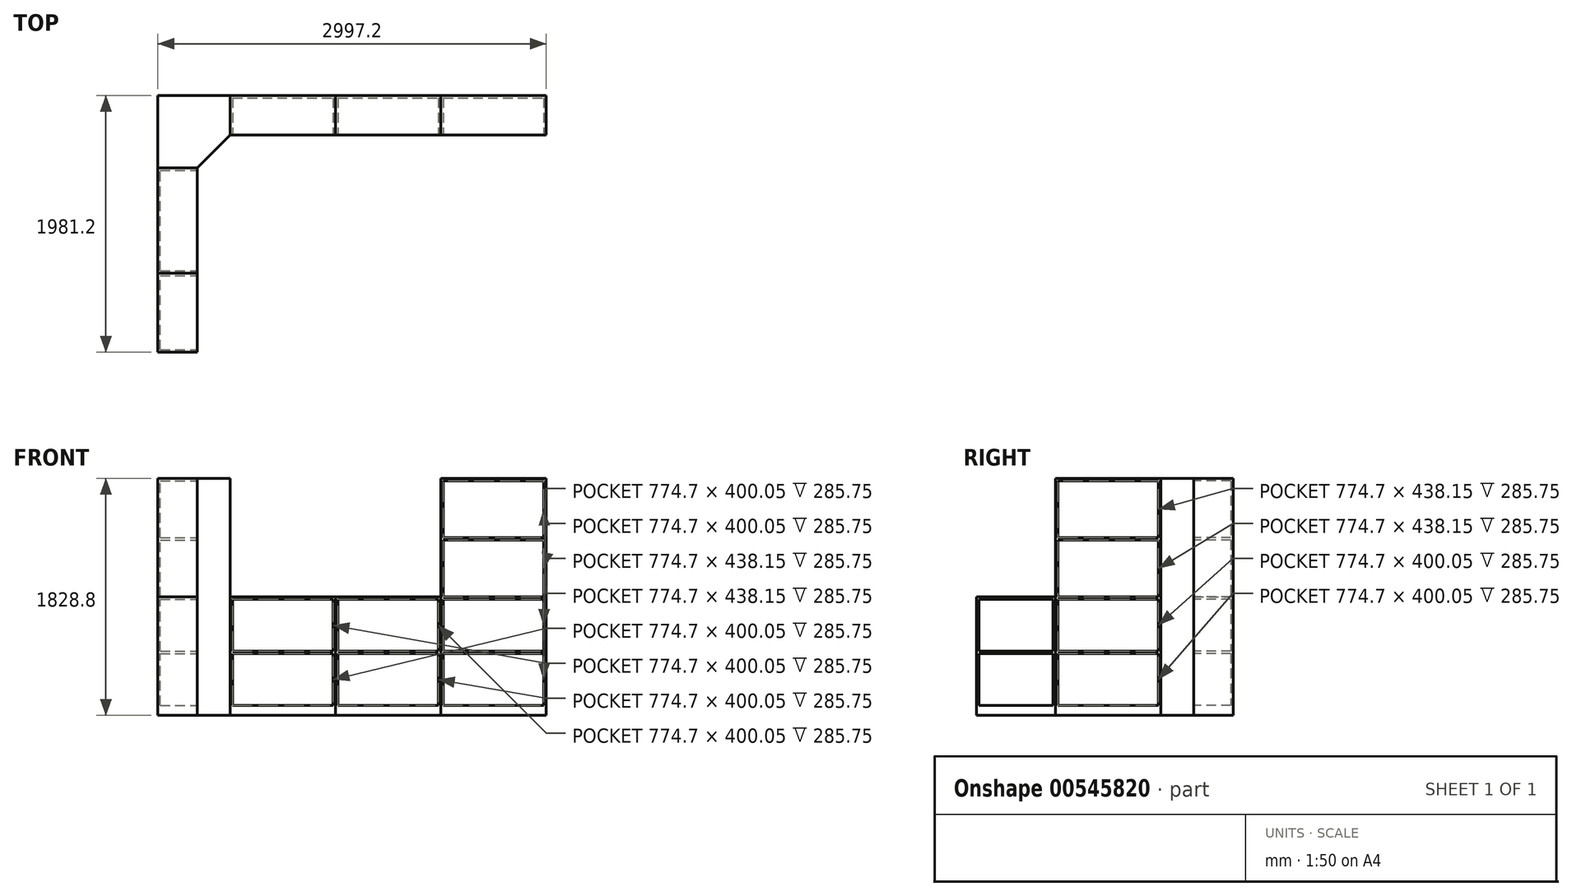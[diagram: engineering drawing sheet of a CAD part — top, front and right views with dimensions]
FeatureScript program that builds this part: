
annotation { "Feature Type Name" : "Feature", "Feature Type Description" : "" }
export const myFeature = defineFeature(function(context is Context, id is Id, definition is map)
    precondition{}
    {
        {
            var Q0;
            Q0=qCreatedBy(makeId("Top.planeOp"),FACE);
            var sketch = newSketch(context, id + "F0", { "sketchPlane" : qUnion([Q0])});
            skLineSegment(sketch, "E0", {"start": v(0, 0) * mm, "end": v(2997.2, 0) * mm});
            skLineSegment(sketch, "E1", {"start": v(0, 0) * mm, "end": v(0, -1981.2) * mm});
            skLineSegment(sketch, "E2", {"start": v(2997.2, 0) * mm, "end": v(2997.2, -304.8) * mm});
            skLineSegment(sketch, "E3", {"start": v(2997.2, -304.8) * mm, "end": v(2184.4, -304.8) * mm});
            skLineSegment(sketch, "E4", {"start": v(2184.4, -304.8) * mm, "end": v(2184.4, 0) * mm});
            skLineSegment(sketch, "E5", {"start": v(2184.4, -304.8) * mm, "end": v(1371.6, -304.8) * mm});
            skLineSegment(sketch, "E6", {"start": v(1371.6, -304.8) * mm, "end": v(1371.6, 0) * mm});
            skLineSegment(sketch, "E7", {"start": v(1371.6, -304.8) * mm, "end": v(558.8, -304.8) * mm});
            skLineSegment(sketch, "E8", {"start": v(558.8, -304.8) * mm, "end": v(558.8, 0) * mm});
            skLineSegment(sketch, "E9", {"start": v(0, -1981.2) * mm, "end": v(304.8, -1981.2) * mm});
            skLineSegment(sketch, "E10", {"start": v(304.8, -1981.2) * mm, "end": v(304.8, -1371.6) * mm});
            skLineSegment(sketch, "E11", {"start": v(304.8, -1371.6) * mm, "end": v(0, -1371.6) * mm});
            skLineSegment(sketch, "E12", {"start": v(304.8, -558.8) * mm, "end": v(0, -558.8) * mm});
            skLineSegment(sketch, "E13", {"start": v(304.8, -1371.6) * mm, "end": v(304.8, -1371.6) * mm});
            skLineSegment(sketch, "E14", {"start": v(304.8, -1371.6) * mm, "end": v(304.8, -558.8) * mm});
            skLineSegment(sketch, "E15", {"start": v(304.8, -558.8) * mm, "end": v(558.8, -304.8) * mm});
            skSolve(sketch);
        }
        {
            var Q0;
            {var subQ0=sQuery(id+"F0.wireOp",EDGE,"E9");Q0=makeQuery(id+"F0.imprint","IMPRINT",FACE,{"disambiguationData":[TD([[makeQuery(id+"F0.imprint","IMPRINT",EDGE,{"derivedFrom":subQ0}),1.0]])]});}
            extrude(context, id + "F1", {"entities" : qUnion([Q0]), "depth" : 914.4 * mm, "offsetDistance" : 25.4 * mm});
        }
        {
            var Q0;
            {var subQ0=sQuery(id+"F0.wireOp",EDGE,"E11");Q0=makeQuery(id+"F0.imprint","IMPRINT",FACE,{"disambiguationData":[TD([[makeQuery(id+"F0.imprint","IMPRINT",EDGE,{"derivedFrom":subQ0}),-1.0]])]});}
            extrude(context, id + "F2", {"entities" : qUnion([Q0]), "depth" : 1828.8 * mm, "offsetDistance" : 25.4 * mm});
        }
        {
            var Q0;
            {var subQ1=sQuery(id+"F0.wireOp",EDGE,"E8");Q0=makeQuery(id+"F0.imprint","IMPRINT",FACE,{"disambiguationData":[TD([[makeQuery(id+"F0.imprint","IMPRINT",EDGE,{"derivedFrom":subQ1}),1.0]])]});}
            extrude(context, id + "F3", {"entities" : qUnion([Q0]), "depth" : 1828.8 * mm, "offsetDistance" : 25.4 * mm});
        }
        {
            var Q0;
            {var subQ0=sQuery(id+"F0.wireOp",EDGE,"E6");Q0=makeQuery(id+"F0.imprint","IMPRINT",FACE,{"disambiguationData":[TD([[makeQuery(id+"F0.imprint","IMPRINT",EDGE,{"derivedFrom":subQ0}),1.0]])]});}
            extrude(context, id + "F4", {"entities" : qUnion([Q0]), "depth" : 914.4 * mm, "offsetDistance" : 25.4 * mm});
        }
        {
            var Q0;
            {var subQ0=sQuery(id+"F0.wireOp",EDGE,"E4");Q0=makeQuery(id+"F0.imprint","IMPRINT",FACE,{"disambiguationData":[TD([[makeQuery(id+"F0.imprint","IMPRINT",EDGE,{"derivedFrom":subQ0}),1.0]])]});}
            extrude(context, id + "F5", {"entities" : qUnion([Q0]), "depth" : 914.4 * mm, "offsetDistance" : 25.4 * mm});
        }
        {
            var Q0;
            {var subQ0=sQuery(id+"F0.wireOp",EDGE,"E2");Q0=makeQuery(id+"F0.imprint","IMPRINT",FACE,{"disambiguationData":[TD([[makeQuery(id+"F0.imprint","IMPRINT",EDGE,{"derivedFrom":subQ0}),-1.0]])]});}
            extrude(context, id + "F6", {"entities" : qUnion([Q0]), "depth" : 1828.8 * mm, "offsetDistance" : 25.4 * mm});
        }
        {
            var Q0;
            Q0=makeQuery(id+"F1.opExtrude","SWEPT_FACE",FACE,{"disambiguationData":[OSD([sQuery(id+"F0.wireOp",EDGE,"E10")])]});
            var sketch = newSketch(context, id + "F7", { "sketchPlane" : qUnion([Q0])});
            skLineSegment(sketch, "E16.bottom", {"start": v(-1962.15, 895.35) * mm, "end": v(-1390.65, 895.35) * mm});
            skLineSegment(sketch, "E16.top", {"start": v(-1962.15, 495.3) * mm, "end": v(-1390.65, 495.3) * mm});
            skLineSegment(sketch, "E16.left", {"start": v(-1962.15, 895.35) * mm, "end": v(-1962.15, 495.3) * mm});
            skLineSegment(sketch, "E16.right", {"start": v(-1390.65, 895.35) * mm, "end": v(-1390.65, 495.3) * mm});
            skLineSegment(sketch, "E17.bottom", {"start": v(-1962.15, 476.25) * mm, "end": v(-1390.65, 476.25) * mm});
            skLineSegment(sketch, "E17.top", {"start": v(-1962.15, 76.2) * mm, "end": v(-1390.65, 76.2) * mm});
            skLineSegment(sketch, "E17.left", {"start": v(-1962.15, 476.25) * mm, "end": v(-1962.15, 76.2) * mm});
            skLineSegment(sketch, "E17.right", {"start": v(-1390.65, 476.25) * mm, "end": v(-1390.65, 76.2) * mm});
            skLineSegment(sketch, "E18.bottom", {"start": v(-1352.55, 76.2) * mm, "end": v(-577.85, 76.2) * mm});
            skLineSegment(sketch, "E18.top", {"start": v(-1352.55, 476.25) * mm, "end": v(-577.85, 476.25) * mm});
            skLineSegment(sketch, "E18.left", {"start": v(-1352.55, 76.2) * mm, "end": v(-1352.55, 476.25) * mm});
            skLineSegment(sketch, "E18.right", {"start": v(-577.85, 76.2) * mm, "end": v(-577.85, 476.25) * mm});
            skLineSegment(sketch, "E19.bottom", {"start": v(-1352.55, 495.3) * mm, "end": v(-577.85, 495.3) * mm});
            skLineSegment(sketch, "E19.top", {"start": v(-1352.55, 895.35) * mm, "end": v(-577.85, 895.35) * mm});
            skLineSegment(sketch, "E19.left", {"start": v(-1352.55, 495.3) * mm, "end": v(-1352.55, 895.35) * mm});
            skLineSegment(sketch, "E19.right", {"start": v(-577.85, 495.3) * mm, "end": v(-577.85, 895.35) * mm});
            skLineSegment(sketch, "E20.bottom", {"start": v(-1352.55, 914.4) * mm, "end": v(-577.85, 914.4) * mm});
            skLineSegment(sketch, "E20.top", {"start": v(-1352.55, 1352.55) * mm, "end": v(-577.85, 1352.55) * mm});
            skLineSegment(sketch, "E20.left", {"start": v(-1352.55, 914.4) * mm, "end": v(-1352.55, 1352.55) * mm});
            skLineSegment(sketch, "E20.right", {"start": v(-577.85, 914.4) * mm, "end": v(-577.85, 1352.55) * mm});
            skLineSegment(sketch, "E21.bottom", {"start": v(-1352.55, 1371.6) * mm, "end": v(-577.85, 1371.6) * mm});
            skLineSegment(sketch, "E21.top", {"start": v(-1352.55, 1809.75) * mm, "end": v(-577.85, 1809.75) * mm});
            skLineSegment(sketch, "E21.left", {"start": v(-1352.55, 1371.6) * mm, "end": v(-1352.55, 1809.75) * mm});
            skLineSegment(sketch, "E21.right", {"start": v(-577.85, 1371.6) * mm, "end": v(-577.85, 1809.75) * mm});
            skSolve(sketch);
        }
        {
            var Q0;
            Q0 = qSketchRegion(id + "F7", true);
            extrude(context, id + "F8", {"entities" : qUnion([Q0]), "operationType" : NewBodyOperationType.REMOVE, "oppositeDirection" : true, "depth" : 285.75 * mm, "offsetDistance" : 25.4 * mm});
        }
        {
            var Q0;
            Q0=makeQuery(id+"F6.opExtrude","SWEPT_FACE",FACE,{"disambiguationData":[OSD([sQuery(id+"F0.wireOp",EDGE,"E3")])]});
            var sketch = newSketch(context, id + "F9", { "sketchPlane" : qUnion([Q0])});
            skLineSegment(sketch, "E22.bottom", {"start": v(577.85, 895.35) * mm, "end": v(1352.55, 895.35) * mm});
            skLineSegment(sketch, "E22.top", {"start": v(577.85, 495.3) * mm, "end": v(1352.55, 495.3) * mm});
            skLineSegment(sketch, "E22.left", {"start": v(577.85, 895.35) * mm, "end": v(577.85, 495.3) * mm});
            skLineSegment(sketch, "E22.right", {"start": v(1352.55, 895.35) * mm, "end": v(1352.55, 495.3) * mm});
            skLineSegment(sketch, "E23.bottom", {"start": v(1390.65, 895.35) * mm, "end": v(2165.35, 895.35) * mm});
            skLineSegment(sketch, "E23.top", {"start": v(1390.65, 495.3) * mm, "end": v(2165.35, 495.3) * mm});
            skLineSegment(sketch, "E23.left", {"start": v(1390.65, 895.35) * mm, "end": v(1390.65, 495.3) * mm});
            skLineSegment(sketch, "E23.right", {"start": v(2165.35, 895.35) * mm, "end": v(2165.35, 495.3) * mm});
            skLineSegment(sketch, "E24.bottom", {"start": v(2203.45, 895.35) * mm, "end": v(2978.15, 895.35) * mm});
            skLineSegment(sketch, "E24.top", {"start": v(2203.45, 495.3) * mm, "end": v(2978.15, 495.3) * mm});
            skLineSegment(sketch, "E24.left", {"start": v(2203.45, 895.35) * mm, "end": v(2203.45, 495.3) * mm});
            skLineSegment(sketch, "E24.right", {"start": v(2978.15, 895.35) * mm, "end": v(2978.15, 495.3) * mm});
            skLineSegment(sketch, "E25.bottom", {"start": v(577.85, 476.25) * mm, "end": v(1352.55, 476.25) * mm});
            skLineSegment(sketch, "E25.top", {"start": v(577.85, 76.2) * mm, "end": v(1352.55, 76.2) * mm});
            skLineSegment(sketch, "E25.left", {"start": v(577.85, 476.25) * mm, "end": v(577.85, 76.2) * mm});
            skLineSegment(sketch, "E25.right", {"start": v(1352.55, 476.25) * mm, "end": v(1352.55, 76.2) * mm});
            skLineSegment(sketch, "E26.bottom", {"start": v(1390.65, 476.25) * mm, "end": v(2165.35, 476.25) * mm});
            skLineSegment(sketch, "E26.top", {"start": v(1390.65, 76.2) * mm, "end": v(2165.35, 76.2) * mm});
            skLineSegment(sketch, "E26.left", {"start": v(1390.65, 476.25) * mm, "end": v(1390.65, 76.2) * mm});
            skLineSegment(sketch, "E26.right", {"start": v(2165.35, 476.25) * mm, "end": v(2165.35, 76.2) * mm});
            skLineSegment(sketch, "E27.bottom", {"start": v(2203.45, 476.25) * mm, "end": v(2978.15, 476.25) * mm});
            skLineSegment(sketch, "E27.top", {"start": v(2203.45, 76.2) * mm, "end": v(2978.15, 76.2) * mm});
            skLineSegment(sketch, "E27.left", {"start": v(2203.45, 476.25) * mm, "end": v(2203.45, 76.2) * mm});
            skLineSegment(sketch, "E27.right", {"start": v(2978.15, 476.25) * mm, "end": v(2978.15, 76.2) * mm});
            skLineSegment(sketch, "E28.bottom", {"start": v(2203.45, 1352.55) * mm, "end": v(2978.15, 1352.55) * mm});
            skLineSegment(sketch, "E28.top", {"start": v(2203.45, 914.4) * mm, "end": v(2978.15, 914.4) * mm});
            skLineSegment(sketch, "E28.left", {"start": v(2203.45, 1352.55) * mm, "end": v(2203.45, 914.4) * mm});
            skLineSegment(sketch, "E28.right", {"start": v(2978.15, 1352.55) * mm, "end": v(2978.15, 914.4) * mm});
            skLineSegment(sketch, "E29.bottom", {"start": v(2203.45, 1809.75) * mm, "end": v(2978.15, 1809.75) * mm});
            skLineSegment(sketch, "E29.top", {"start": v(2203.45, 1371.6) * mm, "end": v(2978.15, 1371.6) * mm});
            skLineSegment(sketch, "E29.left", {"start": v(2203.45, 1809.75) * mm, "end": v(2203.45, 1371.6) * mm});
            skLineSegment(sketch, "E29.right", {"start": v(2978.15, 1809.75) * mm, "end": v(2978.15, 1371.6) * mm});
            skSolve(sketch);
        }
        {
            var Q0;
            Q0 = qSketchRegion(id + "F9", true);
            extrude(context, id + "F10", {"entities" : qUnion([Q0]), "operationType" : NewBodyOperationType.REMOVE, "oppositeDirection" : true, "depth" : 285.75 * mm, "offsetDistance" : 25.4 * mm});
        }
    });
